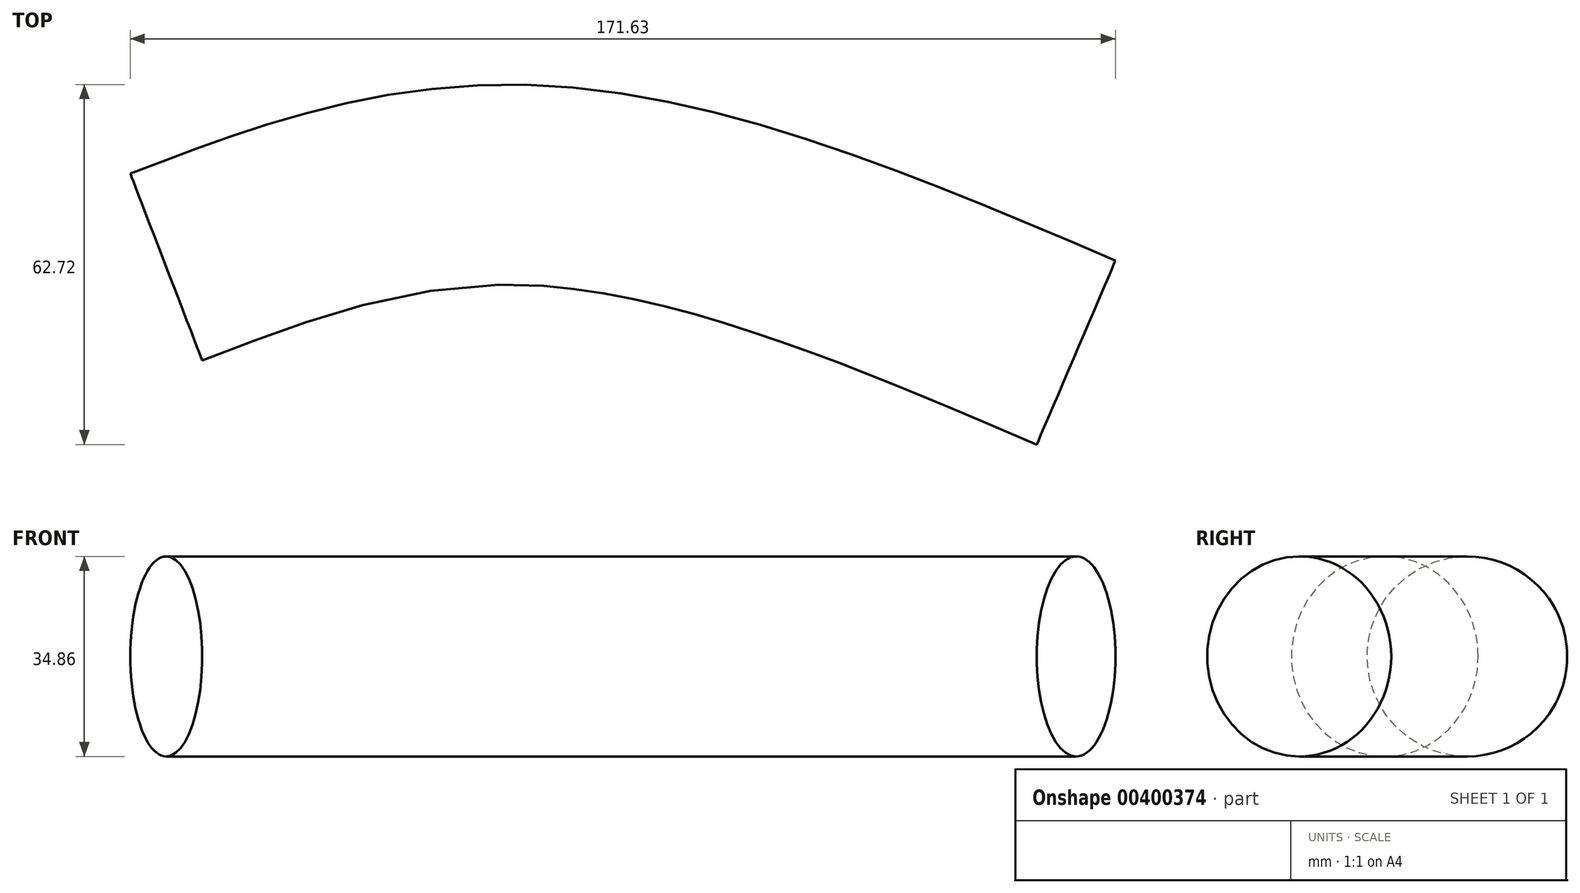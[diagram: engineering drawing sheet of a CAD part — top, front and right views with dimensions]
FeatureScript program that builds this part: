
annotation { "Feature Type Name" : "Feature", "Feature Type Description" : "" }
export const myFeature = defineFeature(function(context is Context, id is Id, definition is map)
    precondition{}
    {
        {
            var Q0;
            Q0=qCreatedBy(makeId("Top.planeOp"),FACE);
            var sketch = newSketch(context, id + "F0", { "sketchPlane" : qUnion([Q0])});
            skFitSpline(sketch, "E0", {"points": [v(-75.83, 14.73) * mm, v(-17.01, 28.25) * mm, v(73.83, 0) * mm], "startDerivative": vector(125.9, 48.49) * mm, "endDerivative": vector(171.7, -73.35) * mm});
            skSolve(sketch);
        }
        {
            var Q0;
            Q0=sQuery(id+"F0.wireOp",VERTEX,"E0.end");
            var Q1;
            Q1=sQuery(id+"F0.wireOp",EDGE,"E0");
            cPlane(context, id + "F1", {"entities" : qUnion([Q0, Q1]), "cplaneType" : CPlaneType.CURVE_POINT, "offset" : 25.4 * mm, "width" : 152.4 * mm, "height" : 152.4 * mm});
        }
        {
            var Q0;
            Q0=qCreatedBy(id+"F1.planeOp",FACE);
            var sketch = newSketch(context, id + "F2", { "sketchPlane" : qUnion([Q0])});
            skCircle(sketch, "E1", {"center": v(40.77, -9.75) * mm, "radius": 17.43 * mm});
            skSolve(sketch);
        }
        {
            var Q0;
            Q0=makeQuery(id+"F2.imprint","IMPRINT",FACE,{"disambiguationData":[TD([[makeQuery(id+"F2.imprint","IMPRINT",EDGE,{"derivedFrom":sQuery(id+"F2.wireOp",EDGE,"E1")}),1.0]])]});
            var Q1;
            Q1=sQuery(id+"F0.wireOp",EDGE,"E0");
            sweep(context, id + "F3", {"profiles" : qUnion([Q0]), "path" : qUnion([Q1])});
        }
    });
